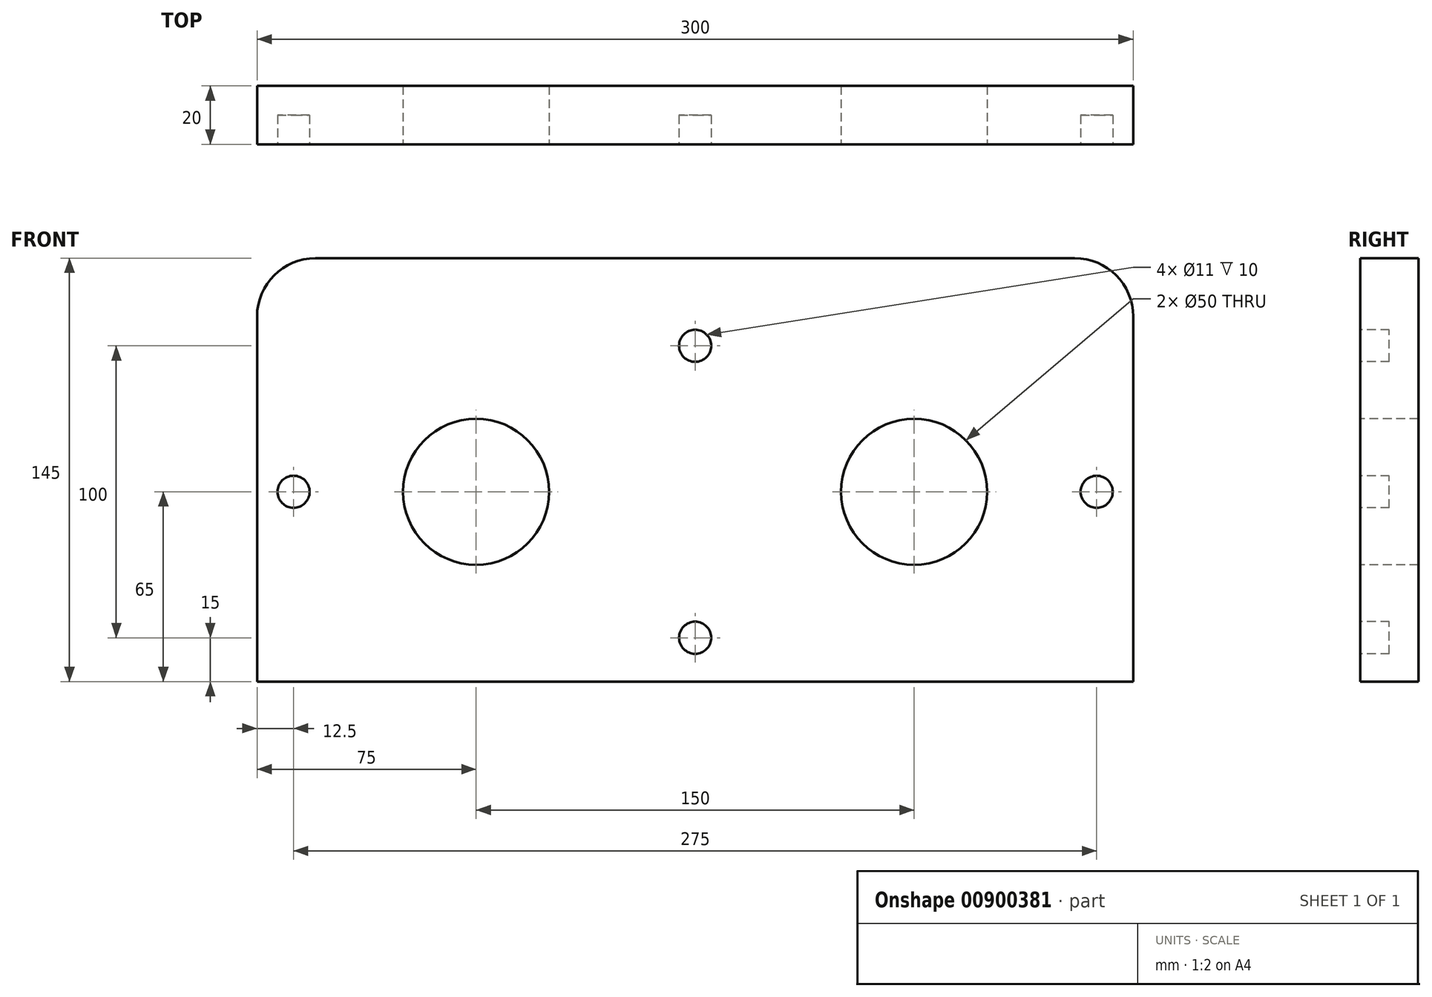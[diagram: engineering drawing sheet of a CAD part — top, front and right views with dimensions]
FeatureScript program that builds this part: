
annotation { "Feature Type Name" : "Feature", "Feature Type Description" : "" }
export const myFeature = defineFeature(function(context is Context, id is Id, definition is map)
    precondition{}
    {
        {
            var Q0;
            Q0=qCreatedBy(makeId("Front.planeOp"),FACE);
            var sketch = newSketch(context, id + "F0", { "sketchPlane" : qUnion([Q0])});
            skLineSegment(sketch, "E0.bottom", {"start": v(-150, 80) * mm, "end": v(150, 80) * mm});
            skLineSegment(sketch, "E0.top", {"start": v(-150, -80) * mm, "end": v(150, -80) * mm});
            skLineSegment(sketch, "E0.left", {"start": v(-150, 80) * mm, "end": v(-150, -80) * mm});
            skLineSegment(sketch, "E0.right", {"start": v(150, 80) * mm, "end": v(150, -80) * mm});
            skPoint(sketch, "E0.middle", {"position": v(0, 0) * mm});
            skSolve(sketch);
        }
        {
            var Q0;
            Q0=qSketchRegion(id+"F0",true);
            extrude(context, id + "F1", {"entities" : qUnion([Q0]), "endBound" : BoundingType.SYMMETRIC, "depth" : 20 * mm, "offsetDistance" : 25 * mm});
        }
        {
            var Q0;
            Q0=makeQuery(id+"F1.opExtrude","CAP_FACE",FACE,{"disambiguationData":[OSD([sQuery(id+"F0.wireOp",EDGE,"E0.bottom"),sQuery(id+"F0.wireOp",EDGE,"E0.top"),sQuery(id+"F0.wireOp",EDGE,"E0.left"),sQuery(id+"F0.wireOp",EDGE,"E0.right")])],"isStart":false});
            var sketch = newSketch(context, id + "F2", { "sketchPlane" : qUnion([Q0])});
            skCircle(sketch, "E1", {"center": v(-75, 0) * mm, "radius": 25 * mm});
            skCircle(sketch, "E2", {"center": v(75, 0) * mm, "radius": 25 * mm});
            skCircle(sketch, "E3", {"center": v(75, 0) * mm, "radius": 75 * mm, "construction": true});
            skCircle(sketch, "E4", {"center": v(-75, 0) * mm, "radius": 75 * mm, "construction": true});
            skSolve(sketch);
        }
        {
            var Q0;
            Q0=qSketchRegion(id+"F2",true);
            extrude(context, id + "F3", {"entities" : qUnion([Q0]), "operationType" : NewBodyOperationType.REMOVE, "endBound" : BoundingType.THROUGH_ALL, "oppositeDirection" : true, "depth" : 25 * mm, "offsetDistance" : 25 * mm});
        }
        {
            var Q0;
            Q0=makeQuery(id+"F1.opExtrude","CAP_FACE",FACE,{"disambiguationData":[OSD([sQuery(id+"F0.wireOp",EDGE,"E0.bottom"),sQuery(id+"F0.wireOp",EDGE,"E0.top"),sQuery(id+"F0.wireOp",EDGE,"E0.left"),sQuery(id+"F0.wireOp",EDGE,"E0.right")])],"isStart":false});
            var sketch = newSketch(context, id + "F4", { "sketchPlane" : qUnion([Q0])});
            skPoint(sketch, "E5", {"position": v(-137.5, 0) * mm});
            skPoint(sketch, "E6", {"position": v(137.5, 0) * mm});
            skPoint(sketch, "E7", {"position": v(0, 50) * mm});
            skPoint(sketch, "E8", {"position": v(0, -50) * mm});
            skLineSegment(sketch, "E9", {"start": v(-137.5, 0) * mm, "end": v(137.5, 0) * mm, "construction": true});
            skLineSegment(sketch, "E10", {"start": v(0, 50) * mm, "end": v(0, -50) * mm, "construction": true});
            skCircle(sketch, "E11", {"center": v(-137.5, 0) * mm, "radius": 5.5 * mm});
            skCircle(sketch, "E12", {"center": v(0, 50) * mm, "radius": 5.5 * mm});
            skCircle(sketch, "E13", {"center": v(137.5, 0) * mm, "radius": 5.5 * mm});
            skCircle(sketch, "E14", {"center": v(0, -50) * mm, "radius": 5.5 * mm});
            skSolve(sketch);
        }
        {
            var Q0;
            Q0 = qSketchRegion(id + "F4", true);
            extrude(context, id + "F5", {"entities" : qUnion([Q0]), "operationType" : NewBodyOperationType.REMOVE, "oppositeDirection" : true, "depth" : 10 * mm, "offsetDistance" : 25 * mm});
        }
        {
            var Q0;
            Q0=makeQuery(id+"F1.opExtrude","CAP_FACE",FACE,{"disambiguationData":[OSD([sQuery(id+"F0.wireOp",EDGE,"E0.bottom"),sQuery(id+"F0.wireOp",EDGE,"E0.top"),sQuery(id+"F0.wireOp",EDGE,"E0.left"),sQuery(id+"F0.wireOp",EDGE,"E0.right")])],"isStart":false});
            var sketch = newSketch(context, id + "F6", { "sketchPlane" : qUnion([Q0])});
            skLineSegment(sketch, "E15.bottom", {"start": v(-150, -65) * mm, "end": v(150, -65) * mm});
            skLineSegment(sketch, "E15.top", {"start": v(-150, -80) * mm, "end": v(150, -80) * mm});
            skLineSegment(sketch, "E15.left", {"start": v(-150, -65) * mm, "end": v(-150, -80) * mm});
            skLineSegment(sketch, "E15.right", {"start": v(150, -65) * mm, "end": v(150, -80) * mm});
            skSolve(sketch);
        }
        {
            var Q0;
            Q0 = qSketchRegion(id + "F6", true);
            extrude(context, id + "F7", {"entities" : qUnion([Q0]), "operationType" : NewBodyOperationType.REMOVE, "endBound" : BoundingType.THROUGH_ALL, "oppositeDirection" : true, "depth" : 25 * mm, "offsetDistance" : 25 * mm});
        }
        {
            var Q0;
            Q0=makeQuery(id+"F1.opExtrude","SWEPT_EDGE",EDGE,{"disambiguationData":[OSD([sQuery(id+"F0.wireOp",EDGE,"E0.bottom"),sQuery(id+"F0.wireOp",EDGE,"E0.left")])]});
            var Q1;
            Q1=makeQuery(id+"F1.opExtrude","SWEPT_EDGE",EDGE,{"disambiguationData":[OSD([sQuery(id+"F0.wireOp",EDGE,"E0.bottom"),sQuery(id+"F0.wireOp",EDGE,"E0.right")])]});
            var Q2;
            Q2=makeQuery(id+"F1.opExtrude","SWEPT_EDGE",EDGE,{"disambiguationData":[OSD([sQuery(id+"F0.wireOp",EDGE,"E0.top"),sQuery(id+"F0.wireOp",EDGE,"E0.left")])]});
            var Q3;
            Q3=makeQuery(id+"F1.opExtrude","SWEPT_EDGE",EDGE,{"disambiguationData":[OSD([sQuery(id+"F0.wireOp",EDGE,"E0.top"),sQuery(id+"F0.wireOp",EDGE,"E0.right")])]});
            var Q4;
            Q4=makeQuery(id+"F7.boolean.opBoolean","COPY",EDGE,{"derivedFrom":makeQuery(id+"F7.opExtrude","SWEPT_EDGE",EDGE,{"disambiguationData":[OSD([sQuery(id+"F0.wireOp",EDGE,"E0.left"),sQuery(id+"F6.wireOp",EDGE,"E15.bottom"),sQuery(id+"F6.wireOp",EDGE,"E15.left")])]})});
            var Q5;
            Q5=makeQuery(id+"F7.boolean.opBoolean","COPY",EDGE,{"derivedFrom":makeQuery(id+"F7.opExtrude","SWEPT_EDGE",EDGE,{"disambiguationData":[OSD([sQuery(id+"F0.wireOp",EDGE,"E0.right"),sQuery(id+"F6.wireOp",EDGE,"E15.bottom"),sQuery(id+"F6.wireOp",EDGE,"E15.right")])]})});
            fillet(context, id + "F8", {"entities" : qUnion([Q0, Q1, Q2, Q3, Q4, Q5]), "radius" : 20 * mm, "tangentPropagation" : true, "allowEdgeOverflow" : false});
        }
    });
